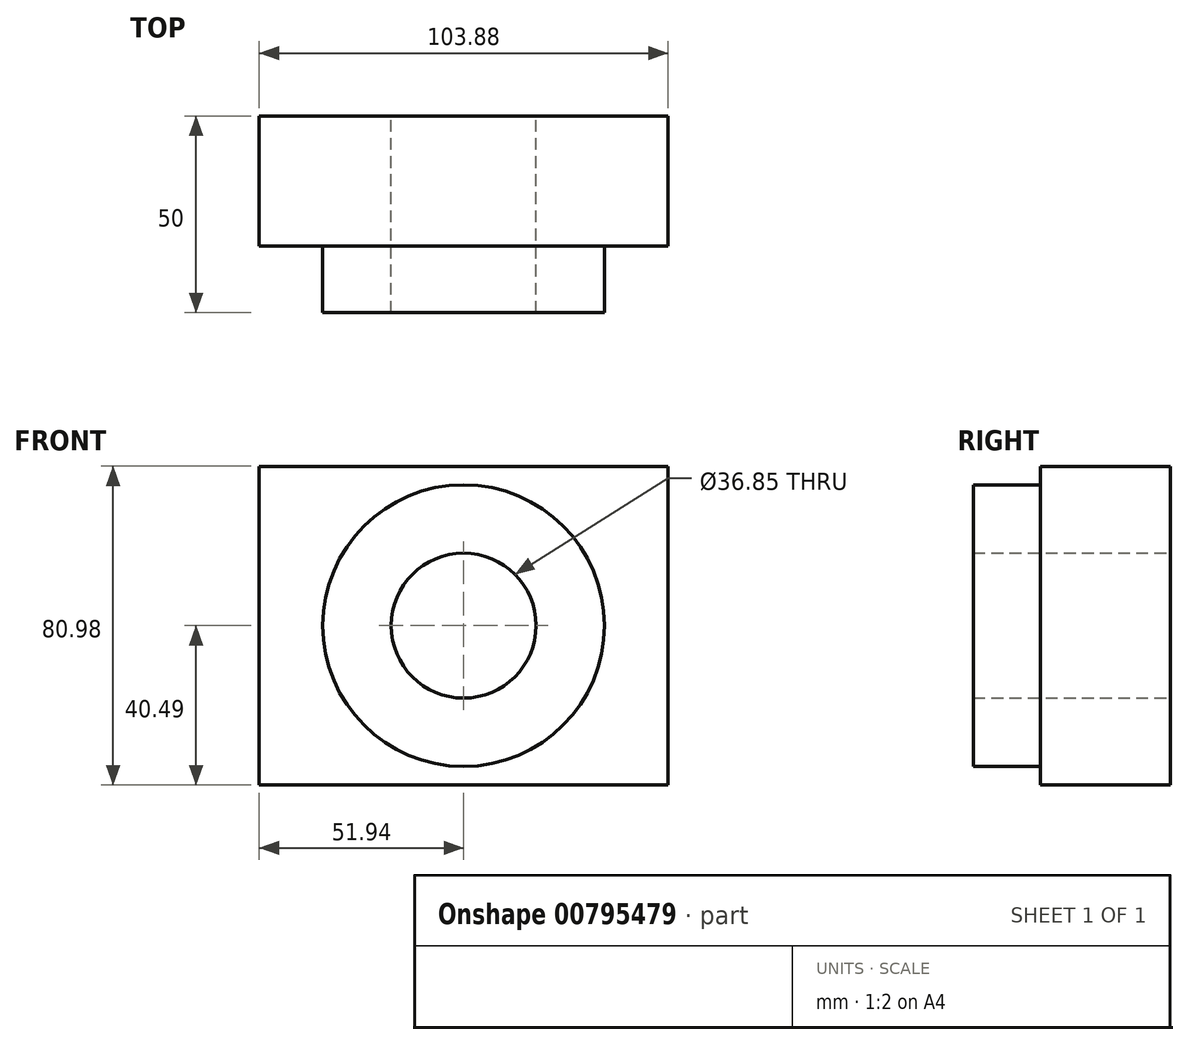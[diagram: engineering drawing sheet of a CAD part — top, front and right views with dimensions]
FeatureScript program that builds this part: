
annotation { "Feature Type Name" : "Feature", "Feature Type Description" : "" }
export const myFeature = defineFeature(function(context is Context, id is Id, definition is map)
    precondition{}
    {
        {
            var Q0;
            Q0=qCreatedBy(makeId("Front.planeOp"),FACE);
            var sketch = newSketch(context, id + "F0", { "sketchPlane" : qUnion([Q0])});
            skLineSegment(sketch, "E0.bottom", {"start": v(-51.94, 40.49) * mm, "end": v(51.94, 40.49) * mm});
            skLineSegment(sketch, "E0.top", {"start": v(-51.94, -40.49) * mm, "end": v(51.94, -40.49) * mm});
            skLineSegment(sketch, "E0.left", {"start": v(-51.94, 40.49) * mm, "end": v(-51.94, -40.49) * mm});
            skLineSegment(sketch, "E0.right", {"start": v(51.94, 40.49) * mm, "end": v(51.94, -40.49) * mm});
            skPoint(sketch, "E0.middle", {"position": v(0, 0) * mm});
            skCircle(sketch, "E1", {"center": v(0, 0) * mm, "radius": 35.78 * mm});
            skCircle(sketch, "E2", {"center": v(0, 0) * mm, "radius": 18.42 * mm});
            skSolve(sketch);
        }
        {
            var Q0;
            Q0=makeQuery(id+"F0.imprint","IMPRINT",FACE,{"disambiguationData":[TD([[makeQuery(id+"F0.imprint","IMPRINT",EDGE,{"derivedFrom":sQuery(id+"F0.wireOp",EDGE,"E1")}),1.0]])]});
            extrude(context, id + "F1", {"entities" : qUnion([Q0]), "depth" : 25 * mm, "offsetDistance" : 25 * mm, "hasSecondDirection" : true, "secondDirectionOppositeDirection" : true, "secondDirectionDepth" : 25 * mm});
        }
        {
            var Q0;
            Q0 = qSketchRegion(id + "F0", true);
            extrude(context, id + "F2", {"entities" : qUnion([Q0]), "operationType" : NewBodyOperationType.ADD, "depth" : 8 * mm, "offsetDistance" : 25 * mm, "hasSecondDirection" : true, "secondDirectionOppositeDirection" : true, "secondDirectionDepth" : 25 * mm});
        }
    });
